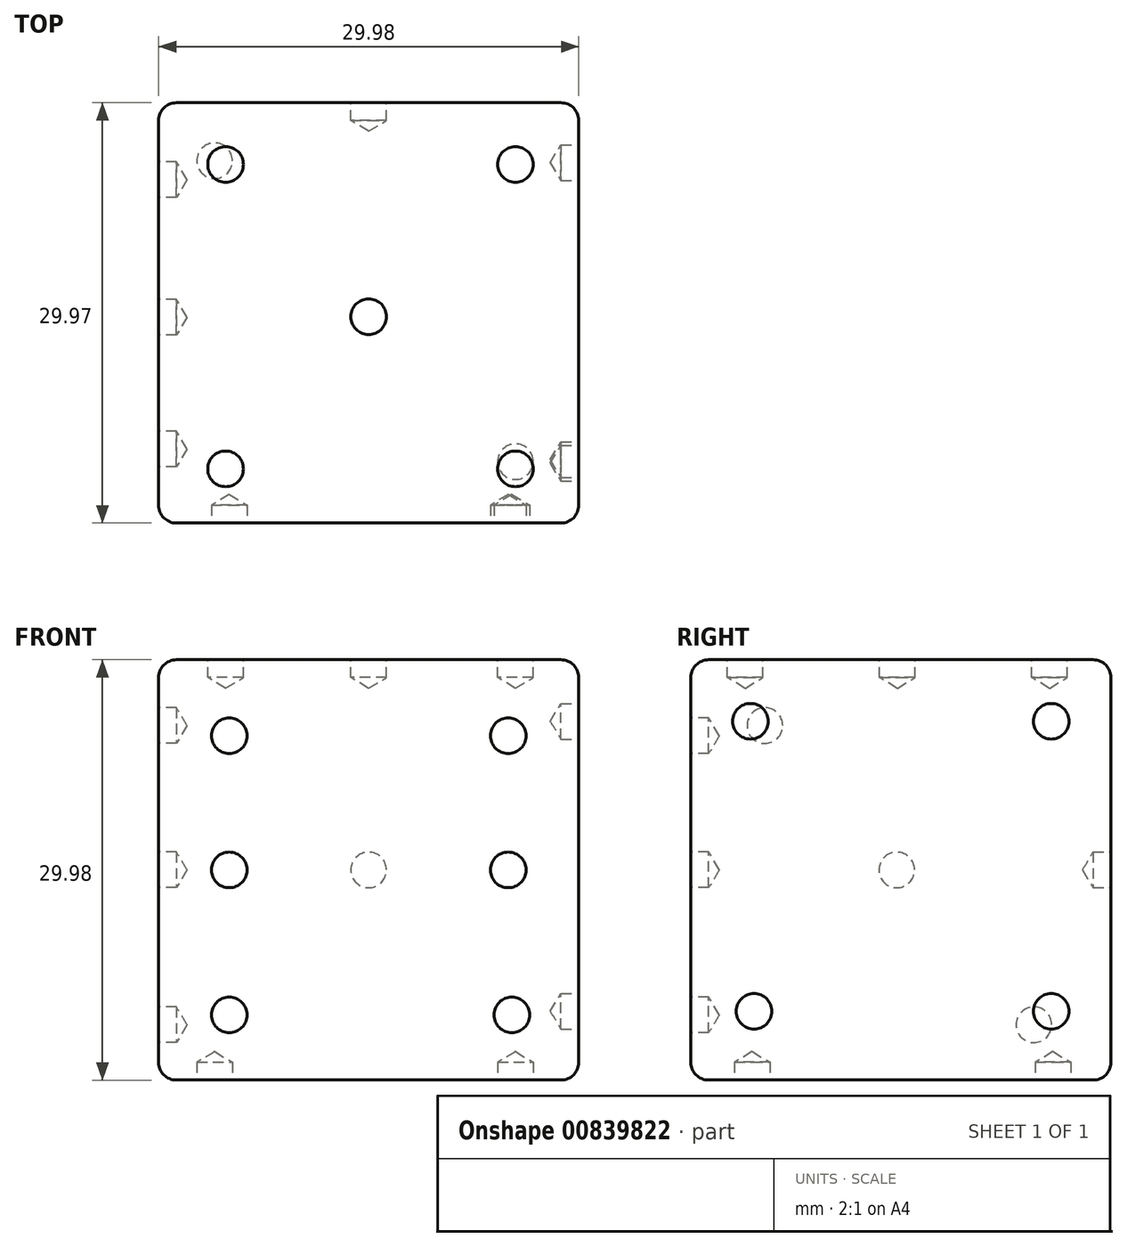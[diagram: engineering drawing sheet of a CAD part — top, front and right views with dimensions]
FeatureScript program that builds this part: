
annotation { "Feature Type Name" : "Feature", "Feature Type Description" : "" }
export const myFeature = defineFeature(function(context is Context, id is Id, definition is map)
    precondition{}
    {
        {
            var Q0;
            Q0=qCreatedBy(makeId("Front.planeOp"),FACE);
            var sketch = newSketch(context, id + "F0", { "sketchPlane" : qUnion([Q0])});
            skLineSegment(sketch, "E0.bottom", {"start": v(14.99, -14.99) * mm, "end": v(-14.99, -14.99) * mm});
            skLineSegment(sketch, "E0.top", {"start": v(14.99, 14.99) * mm, "end": v(-14.99, 14.99) * mm});
            skLineSegment(sketch, "E0.left", {"start": v(14.99, -14.99) * mm, "end": v(14.99, 14.99) * mm});
            skLineSegment(sketch, "E0.right", {"start": v(-14.99, -14.99) * mm, "end": v(-14.99, 14.99) * mm});
            skPoint(sketch, "E0.middle", {"position": v(0, 0) * mm});
            skSolve(sketch);
        }
        {
            var Q0;
            Q0=makeQuery(id+"F0.imprint","IMPRINT",FACE,{"disambiguationData":[TD([[makeQuery(id+"F0.imprint","IMPRINT",EDGE,{"derivedFrom":sQuery(id+"F0.wireOp",EDGE,"E0.bottom")}),-1.0]])]});
            extrude(context, id + "F1", {"entities" : qUnion([Q0]), "depth" : 29.97 * mm, "offsetDistance" : 25.4 * mm});
        }
        {
            var Q0;
            Q0=makeQuery(id+"F1.opExtrude","CAP_FACE",FACE,{"disambiguationData":[OSD([sQuery(id+"F0.wireOp",EDGE,"E0.bottom"),sQuery(id+"F0.wireOp",EDGE,"E0.top"),sQuery(id+"F0.wireOp",EDGE,"E0.left"),sQuery(id+"F0.wireOp",EDGE,"E0.right")])],"isStart":false});
            var sketch = newSketch(context, id + "F2", { "sketchPlane" : qUnion([Q0])});
            skPoint(sketch, "E1", {"position": v(10.21, -10.34) * mm});
            skPoint(sketch, "E2", {"position": v(9.95, 9.57) * mm});
            skPoint(sketch, "E3", {"position": v(-9.95, 9.57) * mm});
            skPoint(sketch, "E4", {"position": v(-9.95, 0) * mm});
            skPoint(sketch, "E5", {"position": v(-9.95, -10.34) * mm});
            skPoint(sketch, "E6", {"position": v(9.95, 0) * mm});
            skSolve(sketch);
        }
        {
            var Q0;
            Q0=sQuery(id+"F2.wireOp",VERTEX,"E3");
            var Q1;
            Q1=sQuery(id+"F2.wireOp",VERTEX,"E4");
            var Q2;
            Q2=sQuery(id+"F2.wireOp",VERTEX,"E5");
            var Q3;
            Q3=sQuery(id+"F2.wireOp",VERTEX,"E1");
            var Q4;
            Q4=sQuery(id+"F2.wireOp",VERTEX,"E6");
            var Q5;
            Q5=sQuery(id+"F2.wireOp",VERTEX,"E2");
            var Q6;
            Q6=makeQuery(id+"F1.opExtrude","SWEPT_BODY",BODY,{"disambiguationData":[OSD([sQuery(id+"F0.wireOp",EDGE,"E0.bottom"),sQuery(id+"F0.wireOp",EDGE,"E0.top"),sQuery(id+"F0.wireOp",EDGE,"E0.left"),sQuery(id+"F0.wireOp",EDGE,"E0.right")])]});
            hole(context, id + "F3", {"style" : HoleStyle.SIMPLE, "endStyle" : HoleEndStyle.BLIND, "holeDiameter" : 2.54 * mm, "majorDiameter" : 6.35 * mm, "holeDepth" : 1.27 * mm, "isTappedThrough" : true, "tappedDepth" : 12.7 * mm, "tapClearance" : 3, "startFromSketch" : true, "locations" : qUnion([Q0, Q1, Q2, Q3, Q4, Q5]), "scope" : qUnion([Q6])});
        }
        {
            var Q0;
            Q0=makeQuery(id+"F1.opExtrude","CAP_FACE",FACE,{"disambiguationData":[OSD([sQuery(id+"F0.wireOp",EDGE,"E0.bottom"),sQuery(id+"F0.wireOp",EDGE,"E0.top"),sQuery(id+"F0.wireOp",EDGE,"E0.left"),sQuery(id+"F0.wireOp",EDGE,"E0.right")])],"isStart":true});
            var sketch = newSketch(context, id + "F4", { "sketchPlane" : qUnion([Q0])});
            skPoint(sketch, "E7", {"position": v(0, 0) * mm});
            skSolve(sketch);
        }
        {
            var Q0;
            Q0=sQuery(id+"F4.wireOp",VERTEX,"E7");
            var Q1;
            Q1=makeQuery(id+"F1.opExtrude","SWEPT_BODY",BODY,{"disambiguationData":[OSD([sQuery(id+"F0.wireOp",EDGE,"E0.bottom"),sQuery(id+"F0.wireOp",EDGE,"E0.top"),sQuery(id+"F0.wireOp",EDGE,"E0.left"),sQuery(id+"F0.wireOp",EDGE,"E0.right")])]});
            hole(context, id + "F5", {"style" : HoleStyle.SIMPLE, "endStyle" : HoleEndStyle.BLIND, "holeDiameter" : 2.54 * mm, "majorDiameter" : 6.35 * mm, "holeDepth" : 1.27 * mm, "isTappedThrough" : true, "tappedDepth" : 12.7 * mm, "tapClearance" : 3, "startFromSketch" : true, "locations" : qUnion([Q0]), "scope" : qUnion([Q1])});
        }
        {
            var Q0;
            Q0=makeQuery(id+"F1.opExtrude","SWEPT_FACE",FACE,{"disambiguationData":[OSD([sQuery(id+"F0.wireOp",EDGE,"E0.left")])]});
            var sketch = newSketch(context, id + "F6", { "sketchPlane" : qUnion([Q0])});
            skPoint(sketch, "E8", {"position": v(-4.27, 10.6) * mm});
            skPoint(sketch, "E9", {"position": v(-4.27, -10.08) * mm});
            skPoint(sketch, "E10", {"position": v(-25.72, 10.6) * mm});
            skPoint(sketch, "E11", {"position": v(-25.46, -10.08) * mm});
            skSolve(sketch);
        }
        {
            var Q0;
            Q0=sQuery(id+"F6.wireOp",VERTEX,"E10");
            var Q1;
            Q1=sQuery(id+"F6.wireOp",VERTEX,"E8");
            var Q2;
            Q2=sQuery(id+"F6.wireOp",VERTEX,"E9");
            var Q3;
            Q3=sQuery(id+"F6.wireOp",VERTEX,"E11");
            var Q4;
            Q4=makeQuery(id+"F1.opExtrude","SWEPT_BODY",BODY,{"disambiguationData":[OSD([sQuery(id+"F0.wireOp",EDGE,"E0.bottom"),sQuery(id+"F0.wireOp",EDGE,"E0.top"),sQuery(id+"F0.wireOp",EDGE,"E0.left"),sQuery(id+"F0.wireOp",EDGE,"E0.right")])]});
            hole(context, id + "F7", {"style" : HoleStyle.SIMPLE, "endStyle" : HoleEndStyle.BLIND, "holeDiameter" : 2.54 * mm, "majorDiameter" : 6.35 * mm, "holeDepth" : 1.27 * mm, "isTappedThrough" : true, "tappedDepth" : 12.7 * mm, "tapClearance" : 3, "startFromSketch" : true, "locations" : qUnion([Q0, Q1, Q2, Q3]), "scope" : qUnion([Q4])});
        }
        {
            var Q0;
            Q0=makeQuery(id+"F1.opExtrude","SWEPT_FACE",FACE,{"disambiguationData":[OSD([sQuery(id+"F0.wireOp",EDGE,"E0.right")])]});
            var sketch = newSketch(context, id + "F8", { "sketchPlane" : qUnion([Q0])});
            skPoint(sketch, "E12", {"position": v(15.29, 0) * mm});
            skPoint(sketch, "E12.positionSnap0", {"position": v(29.97, 0) * mm});
            skPoint(sketch, "E13", {"position": v(5.5, -11.04) * mm});
            skPoint(sketch, "E14", {"position": v(24.7, 10.3) * mm});
            skSolve(sketch);
        }
        {
            var Q0;
            Q0=sQuery(id+"F8.wireOp",VERTEX,"E14");
            var Q1;
            Q1=sQuery(id+"F8.wireOp",VERTEX,"E12");
            var Q2;
            Q2=sQuery(id+"F8.wireOp",VERTEX,"E13");
            var Q3;
            Q3=makeQuery(id+"F1.opExtrude","SWEPT_BODY",BODY,{"disambiguationData":[OSD([sQuery(id+"F0.wireOp",EDGE,"E0.bottom"),sQuery(id+"F0.wireOp",EDGE,"E0.top"),sQuery(id+"F0.wireOp",EDGE,"E0.left"),sQuery(id+"F0.wireOp",EDGE,"E0.right")])]});
            hole(context, id + "F9", {"style" : HoleStyle.SIMPLE, "endStyle" : HoleEndStyle.BLIND, "holeDiameter" : 2.54 * mm, "majorDiameter" : 6.35 * mm, "holeDepth" : 1.27 * mm, "isTappedThrough" : true, "tappedDepth" : 12.7 * mm, "tapClearance" : 3, "startFromSketch" : true, "locations" : qUnion([Q0, Q1, Q2]), "scope" : qUnion([Q3])});
        }
        {
            var Q0;
            Q0=makeQuery(id+"F1.opExtrude","SWEPT_FACE",FACE,{"disambiguationData":[OSD([sQuery(id+"F0.wireOp",EDGE,"E0.bottom")])]});
            var sketch = newSketch(context, id + "F10", { "sketchPlane" : qUnion([Q0])});
            skPoint(sketch, "E15", {"position": v(-10.99, 4.14) * mm});
            skPoint(sketch, "E16", {"position": v(10.47, 25.6) * mm});
            skSolve(sketch);
        }
        {
            var Q0;
            Q0=sQuery(id+"F10.wireOp",VERTEX,"E16");
            var Q1;
            Q1=sQuery(id+"F10.wireOp",VERTEX,"E15");
            var Q2;
            Q2=makeQuery(id+"F1.opExtrude","SWEPT_BODY",BODY,{"disambiguationData":[OSD([sQuery(id+"F0.wireOp",EDGE,"E0.bottom"),sQuery(id+"F0.wireOp",EDGE,"E0.top"),sQuery(id+"F0.wireOp",EDGE,"E0.left"),sQuery(id+"F0.wireOp",EDGE,"E0.right")])]});
            hole(context, id + "F11", {"style" : HoleStyle.SIMPLE, "endStyle" : HoleEndStyle.BLIND, "holeDiameter" : 2.54 * mm, "majorDiameter" : 6.35 * mm, "holeDepth" : 1.27 * mm, "isTappedThrough" : true, "tappedDepth" : 12.7 * mm, "tapClearance" : 3, "startFromSketch" : true, "locations" : qUnion([Q0, Q1]), "scope" : qUnion([Q2])});
        }
        {
            var Q0;
            Q0=makeQuery(id+"F1.opExtrude","SWEPT_FACE",FACE,{"disambiguationData":[OSD([sQuery(id+"F0.wireOp",EDGE,"E0.top")])]});
            var sketch = newSketch(context, id + "F12", { "sketchPlane" : qUnion([Q0])});
            skPoint(sketch, "E17", {"position": v(0, -15.25) * mm});
            skPoint(sketch, "E17.positionSnap0", {"position": v(0, -29.97) * mm});
            skPoint(sketch, "E18", {"position": v(10.47, -4.4) * mm});
            skPoint(sketch, "E19", {"position": v(-10.21, -4.4) * mm});
            skPoint(sketch, "E20", {"position": v(-10.21, -26.1) * mm});
            skPoint(sketch, "E21", {"position": v(10.47, -26.1) * mm});
            skSolve(sketch);
        }
        {
            var Q0;
            Q0=sQuery(id+"F12.wireOp",VERTEX,"E19");
            var Q1;
            Q1=sQuery(id+"F12.wireOp",VERTEX,"E17");
            var Q2;
            Q2=sQuery(id+"F12.wireOp",VERTEX,"E18");
            var Q3;
            Q3=sQuery(id+"F12.wireOp",VERTEX,"E21");
            var Q4;
            Q4=sQuery(id+"F12.wireOp",VERTEX,"E20");
            var Q5;
            Q5=makeQuery(id+"F1.opExtrude","SWEPT_BODY",BODY,{"disambiguationData":[OSD([sQuery(id+"F0.wireOp",EDGE,"E0.bottom"),sQuery(id+"F0.wireOp",EDGE,"E0.top"),sQuery(id+"F0.wireOp",EDGE,"E0.left"),sQuery(id+"F0.wireOp",EDGE,"E0.right")])]});
            hole(context, id + "F13", {"style" : HoleStyle.SIMPLE, "endStyle" : HoleEndStyle.BLIND, "holeDiameter" : 2.54 * mm, "majorDiameter" : 6.35 * mm, "holeDepth" : 1.27 * mm, "isTappedThrough" : true, "tappedDepth" : 12.7 * mm, "tapClearance" : 3, "startFromSketch" : true, "locations" : qUnion([Q0, Q1, Q2, Q3, Q4]), "scope" : qUnion([Q5])});
        }
        {
            var Q0;
            Q0=makeQuery(id+"F1.opExtrude","CAP_EDGE",EDGE,{"disambiguationData":[OSD([sQuery(id+"F0.wireOp",EDGE,"E0.top")])],"isStart":true});
            var Q1;
            Q1=makeQuery(id+"F1.opExtrude","CAP_EDGE",EDGE,{"disambiguationData":[OSD([sQuery(id+"F0.wireOp",EDGE,"E0.left")])],"isStart":true});
            var Q2;
            Q2=makeQuery(id+"F1.opExtrude","CAP_EDGE",EDGE,{"disambiguationData":[OSD([sQuery(id+"F0.wireOp",EDGE,"E0.bottom")])],"isStart":true});
            var Q3;
            Q3=makeQuery(id+"F1.opExtrude","CAP_EDGE",EDGE,{"disambiguationData":[OSD([sQuery(id+"F0.wireOp",EDGE,"E0.right")])],"isStart":true});
            var Q4;
            Q4=makeQuery(id+"F1.opExtrude","SWEPT_EDGE",EDGE,{"disambiguationData":[OSD([sQuery(id+"F0.wireOp",EDGE,"E0.top"),sQuery(id+"F0.wireOp",EDGE,"E0.right")])]});
            var Q5;
            Q5=makeQuery(id+"F1.opExtrude","SWEPT_EDGE",EDGE,{"disambiguationData":[OSD([sQuery(id+"F0.wireOp",EDGE,"E0.top"),sQuery(id+"F0.wireOp",EDGE,"E0.left")])]});
            var Q6;
            Q6=makeQuery(id+"F1.opExtrude","CAP_EDGE",EDGE,{"disambiguationData":[OSD([sQuery(id+"F0.wireOp",EDGE,"E0.top")])],"isStart":false});
            var Q7;
            Q7=makeQuery(id+"F1.opExtrude","CAP_EDGE",EDGE,{"disambiguationData":[OSD([sQuery(id+"F0.wireOp",EDGE,"E0.left")])],"isStart":false});
            var Q8;
            Q8=makeQuery(id+"F1.opExtrude","SWEPT_EDGE",EDGE,{"disambiguationData":[OSD([sQuery(id+"F0.wireOp",EDGE,"E0.bottom"),sQuery(id+"F0.wireOp",EDGE,"E0.left")])]});
            var Q9;
            Q9=makeQuery(id+"F1.opExtrude","CAP_EDGE",EDGE,{"disambiguationData":[OSD([sQuery(id+"F0.wireOp",EDGE,"E0.bottom")])],"isStart":false});
            var Q10;
            Q10=makeQuery(id+"F1.opExtrude","CAP_EDGE",EDGE,{"disambiguationData":[OSD([sQuery(id+"F0.wireOp",EDGE,"E0.right")])],"isStart":false});
            var Q11;
            Q11=makeQuery(id+"F1.opExtrude","SWEPT_EDGE",EDGE,{"disambiguationData":[OSD([sQuery(id+"F0.wireOp",EDGE,"E0.bottom"),sQuery(id+"F0.wireOp",EDGE,"E0.right")])]});
            fillet(context, id + "F14", {"entities" : qUnion([Q0, Q1, Q2, Q3, Q4, Q5, Q6, Q7, Q8, Q9, Q10, Q11]), "radius" : 1.27 * mm, "tangentPropagation" : true, "allowEdgeOverflow" : false});
        }
    });
